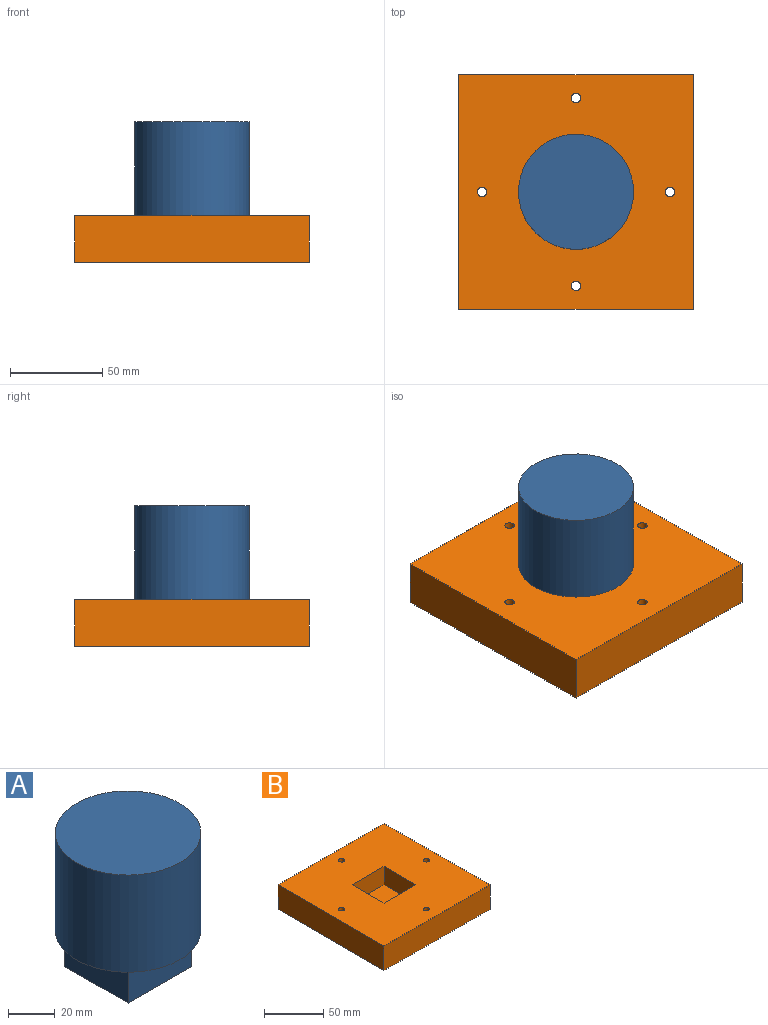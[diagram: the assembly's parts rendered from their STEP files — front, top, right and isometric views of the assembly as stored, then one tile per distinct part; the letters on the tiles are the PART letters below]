
ASSEMBLY  parts=2 mates=1
PART A: 8 faces, bbox 62.2x62.2x69.9 mm
  f0: cylinder r=31.12mm len=62.23mm, axis (0,0,-1), area 9931.5mm2, adj f1,f2
  f1: plane 62.23x62.23mm, normal (0,0,1), area 3041.5mm2, adj f0
  f2: plane 62.23x62.23mm, normal (0,0,-1), area 1589.9mm2, adj f0,f3,f4,f5,f6
  f3: plane 38.1x19.05mm, normal (1,0,0), area 725.8mm2, adj f2,f4,f6,f7
  f4: plane 38.1x19.05mm, normal (0,-1,0), area 725.8mm2, adj f2,f3,f5,f7
  f5: plane 38.1x19.05mm, normal (-1,0,0), area 725.8mm2, adj f2,f4,f6,f7
  f6: plane 38.1x19.05mm, normal (0,1,0), area 725.8mm2, adj f2,f3,f5,f7
  f7: plane 38.1x38.1mm, normal (0,0,-1), area 1451.6mm2, adj f3,f4,f5,f6
PART B: 15 faces, bbox 127x127x25.4 mm
  f0: plane 127x127mm, normal (0,0,1), area 14595.5mm2, adj f1,f2,f3,f4,f5,f6,f7,f8
  f1: plane 127x25.4mm, normal (0,1,0), area 3225.8mm2, adj f0,f2,f8,f9
  f2: plane 127x25.4mm, normal (-1,0,0), area 3225.8mm2, adj f0,f1,f3,f9
  f3: plane 127x25.4mm, normal (0,-1,0), area 3225.8mm2, adj f0,f2,f8,f9
  f4: cylinder r=2.55mm len=25.4mm, axis (0,0,-1), area 407.4mm2, adj f0,f9
  f5: cylinder r=2.55mm len=25.4mm, axis (0,0,-1), area 407.4mm2, adj f0,f9
  f6: cylinder r=2.55mm len=25.4mm, axis (0,0,-1), area 407.4mm2, adj f0,f9
  f7: cylinder r=2.55mm len=25.4mm, axis (0,0,-1), area 407.4mm2, adj f0,f9
  f8: plane 127x25.4mm, normal (1,0,0), area 3225.8mm2, adj f0,f1,f3,f9
  f9: plane 127x127mm, normal (0,0,-1), area 16047.1mm2, adj f1,f2,f3,f4,f5,f6,f7,f8
  f10: plane 38.1x19.05mm, normal (-1,0,0), area 725.8mm2, adj f0,f11,f13,f14
  f11: plane 38.1x19.05mm, normal (0,-1,0), area 725.8mm2, adj f0,f10,f12,f14
  f12: plane 38.1x19.05mm, normal (1,0,0), area 725.8mm2, adj f0,f11,f13,f14
  f13: plane 38.1x19.05mm, normal (0,1,0), area 725.8mm2, adj f0,f10,f12,f14
  f14: plane 38.1x38.1mm, normal (0,0,1), area 1451.6mm2, adj f10,f11,f12,f13
PLACE A t=(-88.83,-20.15,76.04)mm
PLACE B t=(-88.83,-20.15,50.64)mm
MATE fastened B.f14 <-> A.f0  axis (0,0,1) through (-88.83,-20.15,56.99)mm
